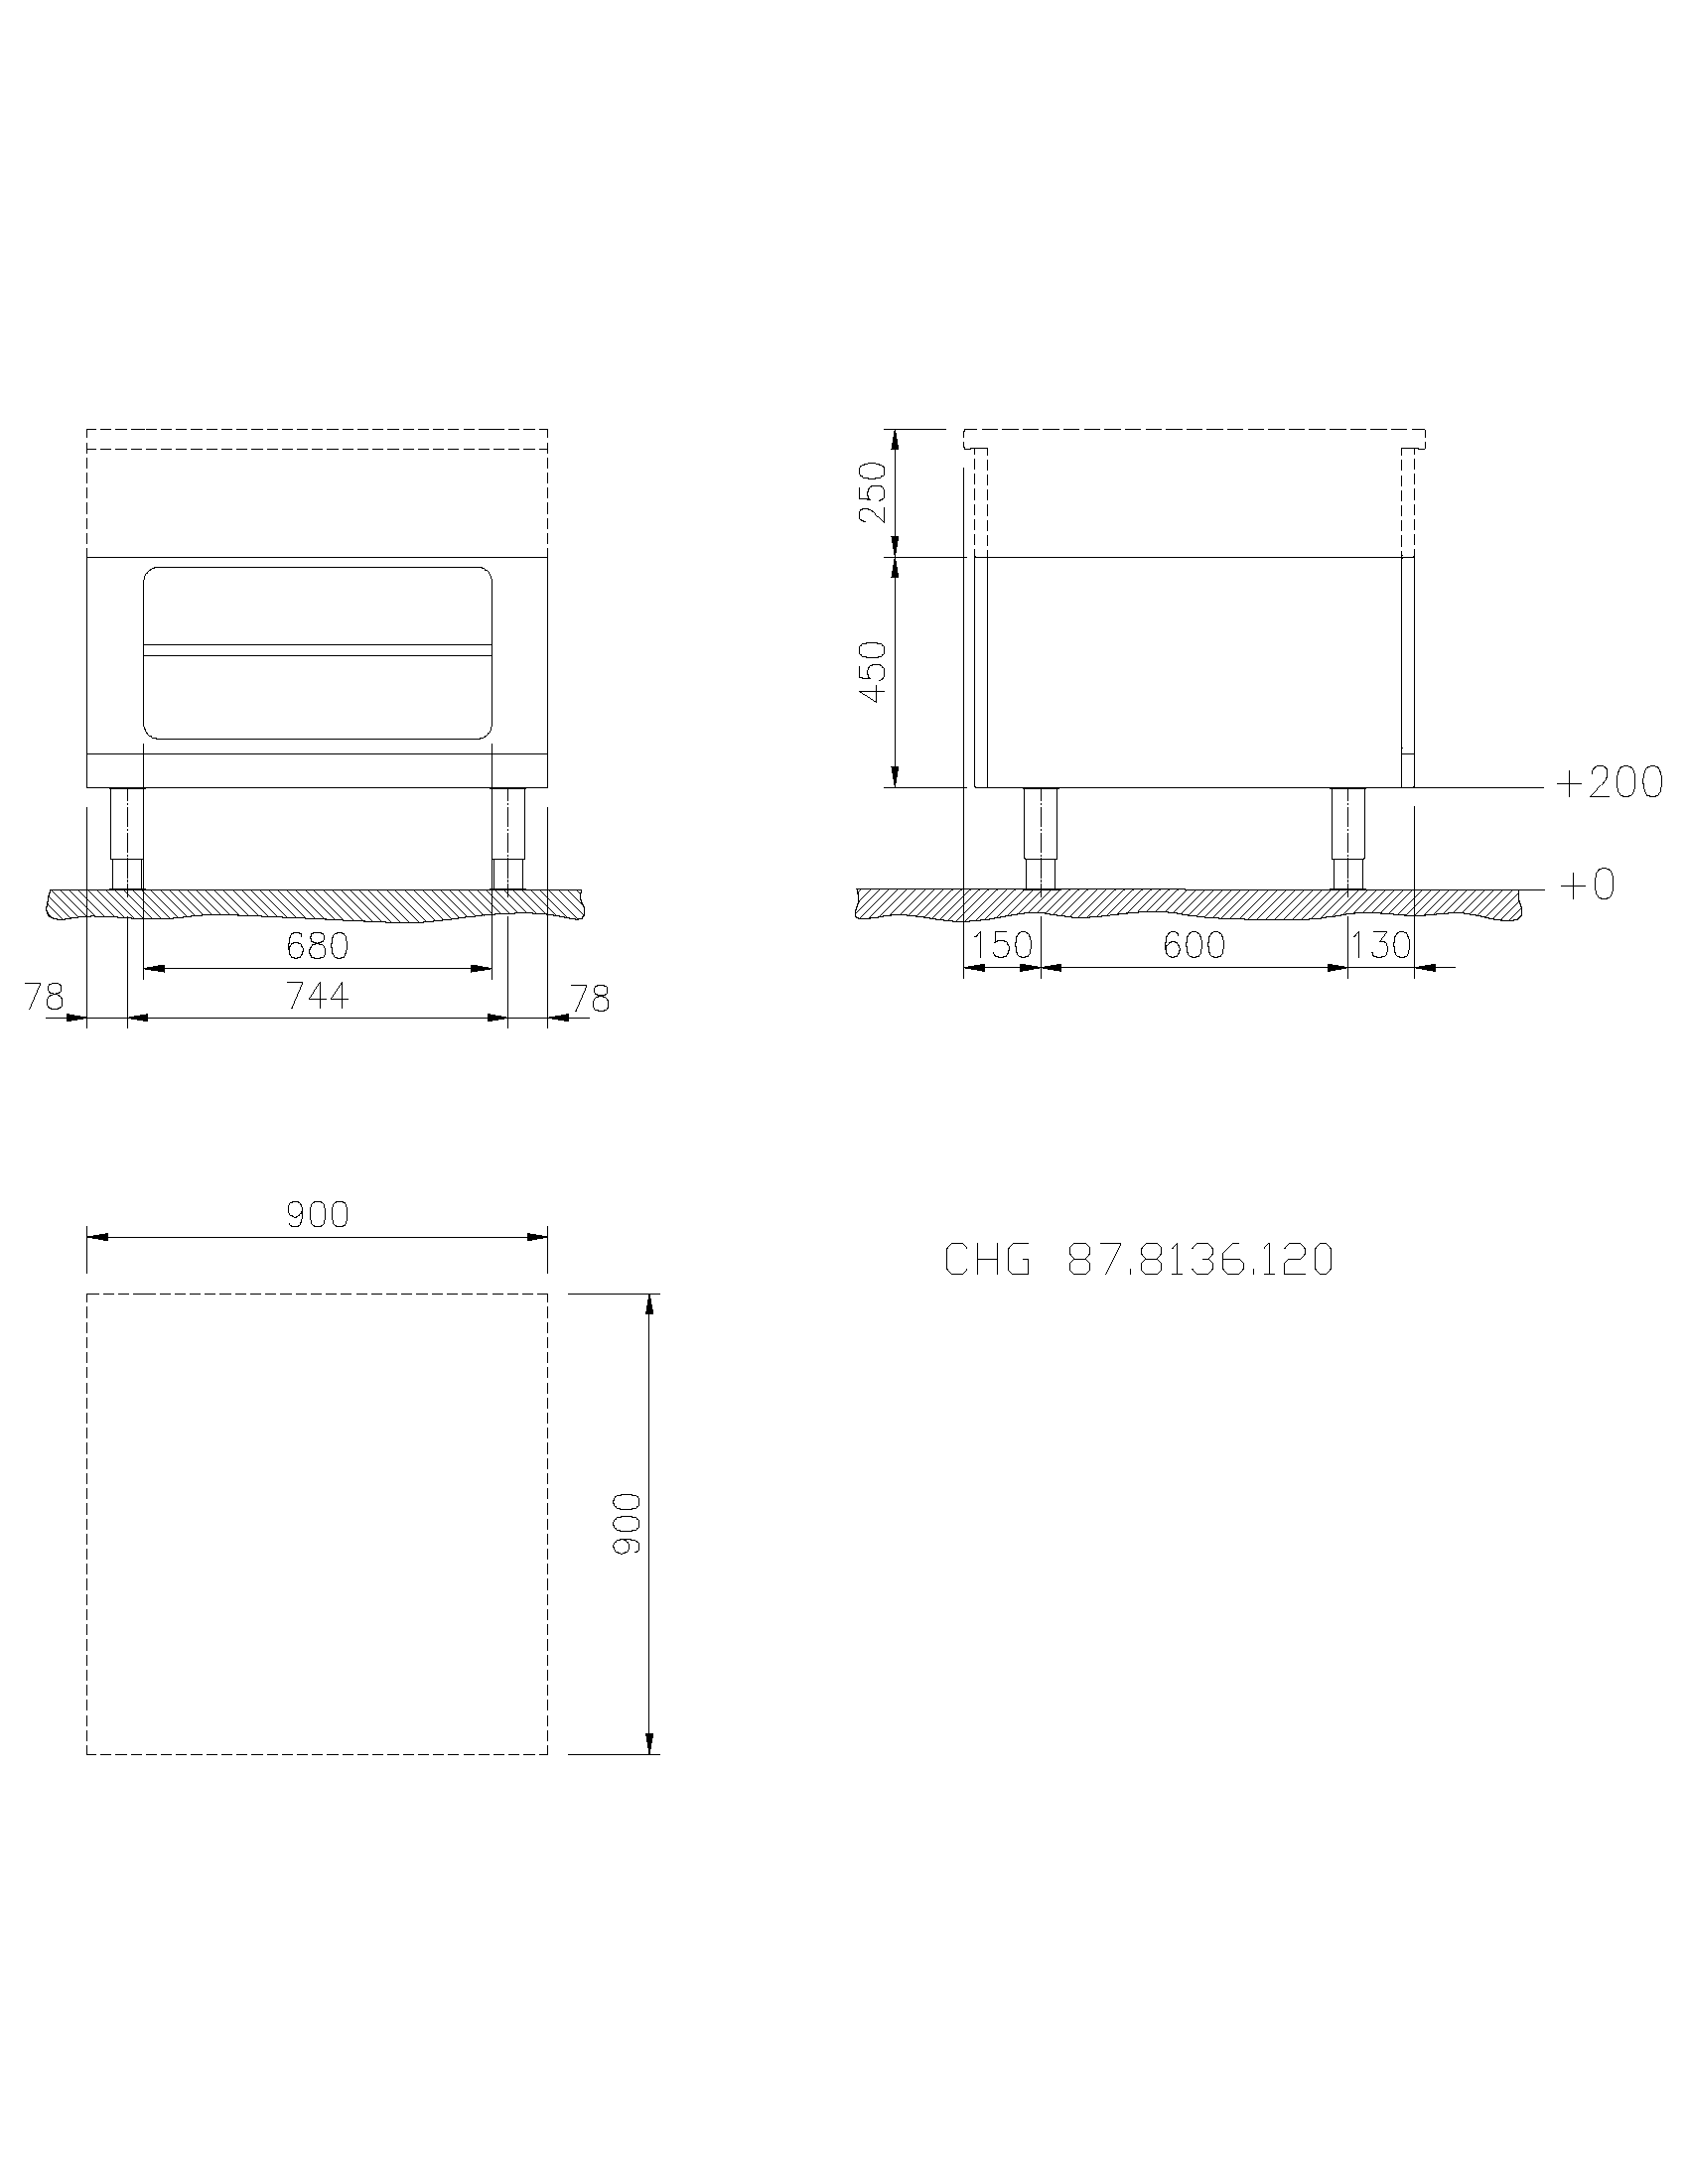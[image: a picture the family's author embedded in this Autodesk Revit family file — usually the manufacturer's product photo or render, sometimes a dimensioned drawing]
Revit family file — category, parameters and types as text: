
# Revit family: QF_ELECTROLUXPROFESSIONAL_589826_MCFCEAEDDM
name_source: partatom
category: Attrezzature speciali
units: mm (PartAtom-declared; Revit-internal decimal feet)

## family parameters
Basato su piano di lavoro = No
Condiviso = No
Punto di calcolo locali = No
Quota connettore circolare = Usa diametro
Sempre verticale = Sì
Taglio con vuoti quando caricato = No
Tipo di parte = Normale

## types (1)
- Standard
    Accessory = Sì
    Cold Water Size = 0"
    Compressed Air Pressure = 0.00 psi
    Compressed Air Size = 0"
    Compressed Air Volume = 0 GPM
    Condensate Return Size = 0"
    Cycle = 50 Hz
    Depth Actual = 900 mm  [stored 2.95276 ft]
    Descrizione = DEEP FRYER,1X23L,1S,500X900X700H MARINE
    Direct Waste Size = 0"
    Gas Input Pressure = 0.0
    Gas KW = 0
    Gas Size = 0"
    HP = 24.1 HP
    Height Actual = 700 mm  [stored 2.29659 ft]
    Hot Water Size = 0"
    Item Number = 589826
    Length Actual = 500 mm  [stored 1.64042 ft]
    Modello = MCFCEAEDDM
    Phase = 3
    Produttore = Electrolux Professional
    Prospetto di default = 0 mm  [stored 0 ft]
    Refrigerant Compressor Remote = Sì
    Refrigeration Liquid Line Size = 0 mm  [stored 0 ft]
    Refrigeration Suction Line Size = 0 mm  [stored 0 ft]
    Steam Consumption per Hour = 0
    Steam Supply Maximum Pressure = 0.00 psi
    Steam Supply Minimum Pressure = 0.00 psi
    Steam Supply Size = 0"
    URL = https://www.electroluxprofessional.com
    URL Manufacturer = https://www.electroluxprofessional.com
    Volts = 440 V
    Watts = 18000 W
    Weight = 85.00 kg

note: source unit labels omitted for Gas Input Pressure — the stored unit's dimension contradicts the parameter name (converter mislabeling)

note: [stored X ft] marks values corroborated as IEEE doubles in the binary element streams (Revit-internal decimal feet)

## geometry (parser evidence)
native form markers: Blend x4, Sweep x10
no freeform markers — native parametric forms only
